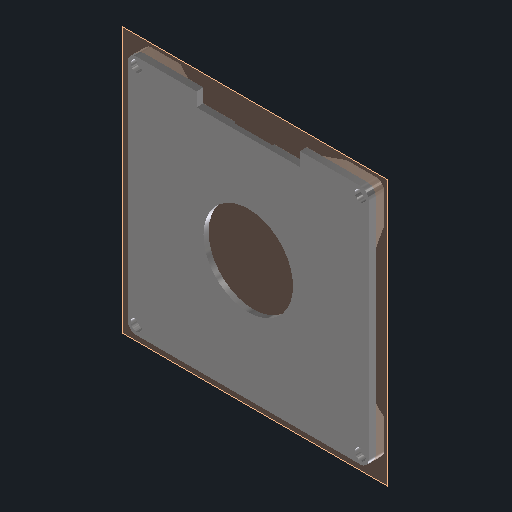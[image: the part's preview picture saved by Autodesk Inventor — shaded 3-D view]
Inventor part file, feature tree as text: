
AUTODESK INVENTOR PART (.ipt)
format: ipt  version: 2022 (Build 260153000, 153)  size: 164,864 bytes
history: native  units: mm
features: reference x12, sketch x4, other x4, plane x3, extrude x3, chamfer x1, hole x1
ambient origin geometry x8: Origin, YZ Plane, XZ Plane, XY Plane, X Axis, Y Axis, Z Axis, Center Point
bodies: Solid1 (feature_tree)
feature tree (28):
  plane  "Work Plane1"
  sketch  "Sketch1"  dims[d0=1.0mm d1=4.0mm d2=0.0mm]
  plane  "Work Plane2"
  extrude  "Extrusion1"  Depth=4.0mm TaperAngle=0.0deg
  extrude  "Extrusion2"  Depth=1.0mm TaperAngle=0.0deg
  sketch  "Sketch3"  dims[d6=4.0mm d7=0.0mm d8=5.0mm d9=2.0mm d10=45.0deg]
  plane  "Work Plane3"
  extrude  "Extrusion3"  Depth=5.0mm TaperAngle=45.0deg
  chamfer  "Chamfer1"  [1 undecoded]
  hole  "Hole1"  [1 undecoded]
  reference  "Reference1"
  reference  "Reference2"
  reference  "Reference3"
  sketch  "Sketch2"  dims[d3=2.0mm d4=1.0mm d5=0.0mm]
  reference  "Reference4"
  reference  "Reference5"
  reference  "Reference6"
  reference  "Reference7"
  reference  "Reference8"
  sketch  "Sketch4"  dims[d11=3.4mm d12=6.0mm d13=6.5mm d14=3.4mm d15=14.3117mm d16=8.8mm d17=20.594885mm]
  reference  "Reference9"
  reference  "Reference10"
  reference  "Reference11"
  reference  "Reference12"
  other  "SistemaDeElevación.iam"
  other  "soporte de rodamientos:1"
  other  "Montura de Motor:1"
  other  "BridaTornillo:1"
note: 2 required parameter values undecoded (feature->parameter linkage not recoverable at this tier; creation-order binding heuristic only, values carry confidence <= 0.55)
